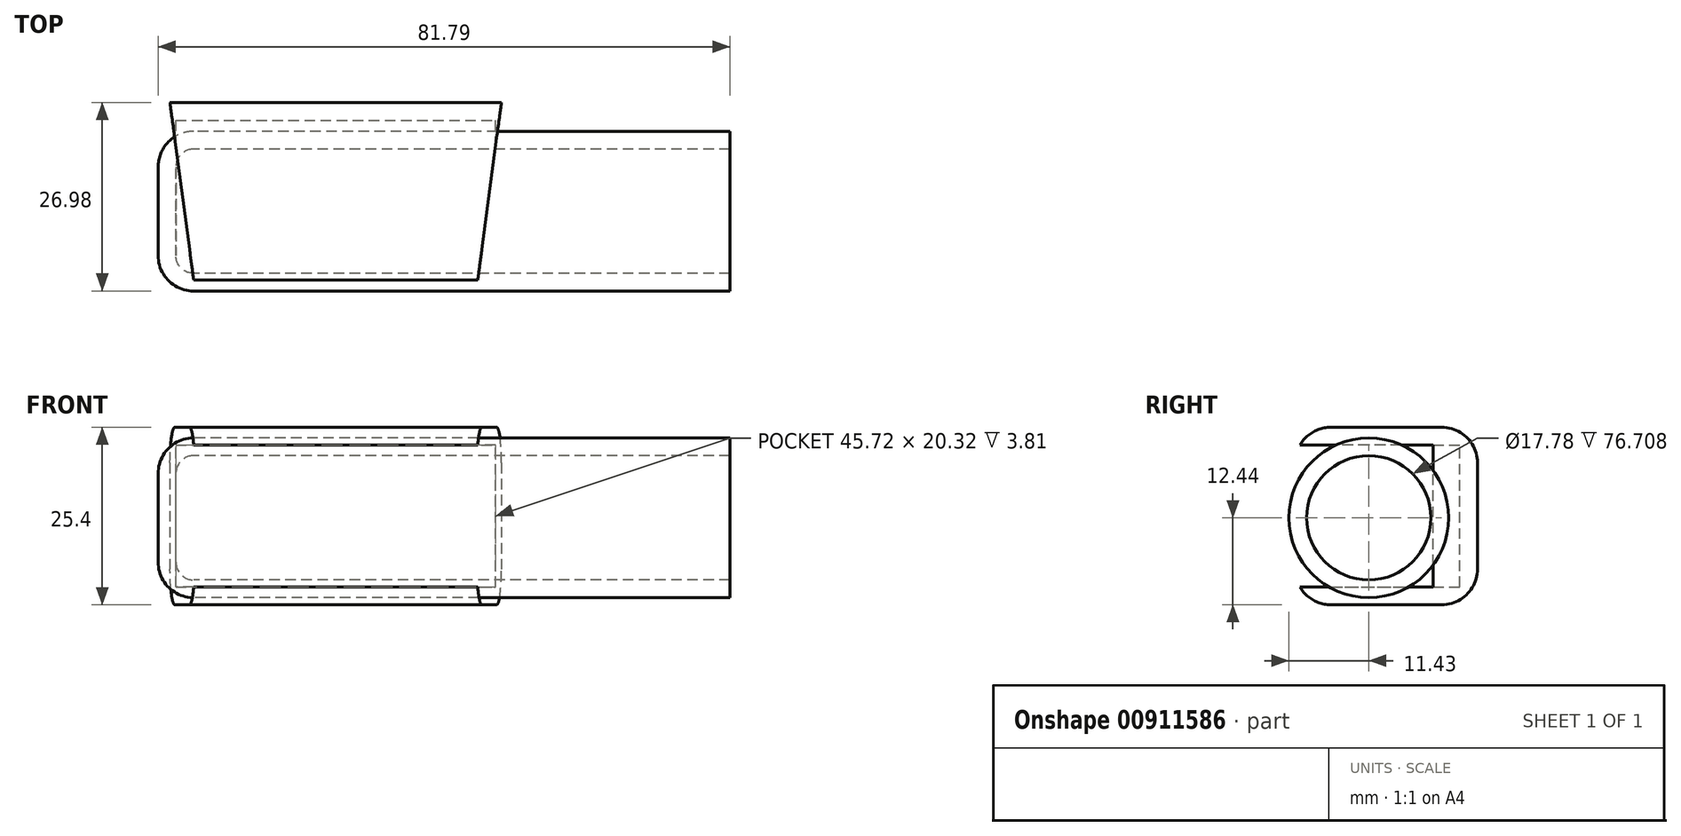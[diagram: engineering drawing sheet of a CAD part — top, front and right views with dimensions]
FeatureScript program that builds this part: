
annotation { "Feature Type Name" : "Feature", "Feature Type Description" : "" }
export const myFeature = defineFeature(function(context is Context, id is Id, definition is map)
    precondition{}
    {
        {
            var Q0;
            Q0=qCreatedBy(makeId("Front.planeOp"),FACE);
            var sketch = newSketch(context, id + "F0", { "sketchPlane" : qUnion([Q0])});
            skLineSegment(sketch, "E0.bottom", {"start": v(0, 0) * mm, "end": v(50.8, 0) * mm});
            skLineSegment(sketch, "E0.top", {"start": v(0, 25.4) * mm, "end": v(50.8, 25.4) * mm});
            skLineSegment(sketch, "E0.left", {"start": v(0, 0) * mm, "end": v(0, 25.4) * mm});
            skLineSegment(sketch, "E0.right", {"start": v(50.8, 0) * mm, "end": v(50.8, 25.4) * mm});
            skSolve(sketch);
        }
        {
            var Q0;
            Q0=makeQuery(id+"F0.imprint","IMPRINT",FACE,{"disambiguationData":[TD([[makeQuery(id+"F0.imprint","IMPRINT",EDGE,{"derivedFrom":sQuery(id+"F0.wireOp",EDGE,"E0.bottom")}),1.0]])]});
            extrude(context, id + "F1", {"entities" : qUnion([Q0]), "depth" : 25.4 * mm, "offsetDistance" : 25.4 * mm});
        }
        {
            var Q0;
            Q0=makeQuery(id+"F1.opExtrude","CAP_FACE",FACE,{"disambiguationData":[OSD([sQuery(id+"F0.wireOp",EDGE,"E0.bottom"),sQuery(id+"F0.wireOp",EDGE,"E0.top"),sQuery(id+"F0.wireOp",EDGE,"E0.left"),sQuery(id+"F0.wireOp",EDGE,"E0.right")])],"isStart":false});
            shell(context, id + "F2", {"entities" : qUnion([Q0]), "thickness" : 2.54 * mm});
        }
        {
            var Q0;
            Q0=makeQuery(id+"F1.opExtrude","CAP_EDGE",EDGE,{"disambiguationData":[OSD([sQuery(id+"F0.wireOp",EDGE,"E0.right")])],"isStart":false});
            var Q1;
            Q1=makeQuery(id+"F1.opExtrude","CAP_EDGE",EDGE,{"disambiguationData":[OSD([sQuery(id+"F0.wireOp",EDGE,"E0.left")])],"isStart":false});
            chamfer(context, id + "F3", {"entities" : qUnion([Q0, Q1]), "chamferType" : ChamferType.TWO_OFFSETS, "width1" : 5.08 * mm, "oppositeDirection" : false, "width2" : 38.1 * mm, "tangentPropagation" : true});
        }
        {
            var Q0;
            Q0=makeQuery(id+"F1.opExtrude","CAP_EDGE",EDGE,{"disambiguationData":[OSD([sQuery(id+"F0.wireOp",EDGE,"E0.top")])],"isStart":true});
            var Q1;
            Q1=makeQuery(id+"F1.opExtrude","CAP_EDGE",EDGE,{"disambiguationData":[OSD([sQuery(id+"F0.wireOp",EDGE,"E0.bottom")])],"isStart":true});
            var Q2;
            Q2=makeQuery(id+"F1.opExtrude","CAP_EDGE",EDGE,{"disambiguationData":[OSD([sQuery(id+"F0.wireOp",EDGE,"E0.bottom")])],"isStart":false});
            var Q3;
            Q3=makeQuery(id+"F1.opExtrude","CAP_EDGE",EDGE,{"disambiguationData":[OSD([sQuery(id+"F0.wireOp",EDGE,"E0.top")])],"isStart":false});
            fillet(context, id + "F4", {"entities" : qUnion([Q0, Q1, Q2, Q3]), "radius" : 5.08 * mm, "tangentPropagation" : true, "allowEdgeOverflow" : false});
        }
        {
            var Q0;
            Q0=qCreatedBy(makeId("Right.planeOp"),FACE);
            var sketch = newSketch(context, id + "F5", { "sketchPlane" : qUnion([Q0])});
            skCircle(sketch, "E1", {"center": v(-15.55, 12.44) * mm, "radius": 11.43 * mm});
            skSolve(sketch);
        }
        {
            var Q0;
            Q0=makeQuery(id+"F5.imprint","IMPRINT",FACE,{"disambiguationData":[TD([[makeQuery(id+"F5.imprint","IMPRINT",EDGE,{"derivedFrom":sQuery(id+"F5.wireOp",EDGE,"E1")}),1.0]])]});
            extrude(context, id + "F6", {"entities" : qUnion([Q0]), "depth" : 81.8 * mm, "offsetDistance" : 25.4 * mm});
        }
        {
            var Q0;
            Q0=makeQuery(id+"F6.opExtrude","CAP_FACE",FACE,{"disambiguationData":[OSD([sQuery(id+"F5.wireOp",EDGE,"E1")])],"isStart":true});
            fillet(context, id + "F7", {"entities" : qUnion([Q0]), "radius" : 5.08 * mm, "tangentPropagation" : true, "allowEdgeOverflow" : false});
        }
        {
            var Q0;
            Q0=makeQuery(id+"F6.opExtrude","CAP_FACE",FACE,{"disambiguationData":[OSD([sQuery(id+"F5.wireOp",EDGE,"E1")])],"isStart":false});
            shell(context, id + "F8", {"entities" : qUnion([Q0]), "thickness" : 2.54 * mm});
        }
    });
